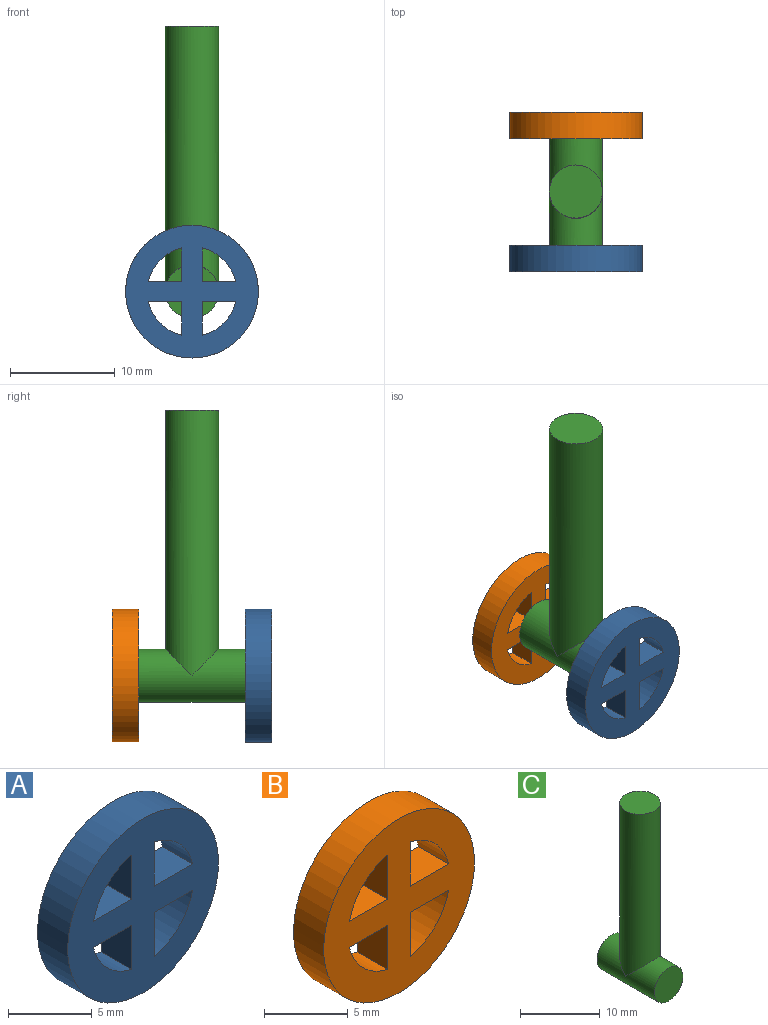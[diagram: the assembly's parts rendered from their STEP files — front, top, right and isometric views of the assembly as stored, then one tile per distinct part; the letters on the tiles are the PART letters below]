
ASSEMBLY  parts=3 mates=2
PART A: 15 faces, bbox 12.7x2.5x12.7 mm
  f0: cylinder r=4.28mm len=3.22mm, axis (0,1,0), area 12.2mm2, adj f1,f12,f13,f14
  f1: plane 3.22x2.54mm, normal (0,0,1), area 8.2mm2, adj f0,f12,f13,f14
  f2: cylinder r=4.28mm len=3.22mm, axis (0,1,0), area 12.2mm2, adj f3,f9,f13,f14
  f3: plane 3.22x2.54mm, normal (-1,0,0), area 8.2mm2, adj f2,f9,f13,f14
  f4: plane 3.22x2.54mm, normal (0,0,-1), area 8.2mm2, adj f5,f10,f13,f14
  f5: cylinder r=4.28mm len=3.22mm, axis (0,1,0), area 12.2mm2, adj f4,f10,f13,f14
  f6: cylinder r=4.28mm len=3.22mm, axis (0,1,0), area 12.2mm2, adj f7,f11,f13,f14
  f7: plane 3.22x2.54mm, normal (0,0,-1), area 8.2mm2, adj f6,f11,f13,f14
  f8: cylinder r=6.35mm len=12.7mm, axis (0,1,0), area 101.3mm2, adj f13,f14
  f9: plane 3.22x2.54mm, normal (0,0,1), area 8.2mm2, adj f2,f3,f13,f14
  f10: plane 3.22x2.54mm, normal (1,0,0), area 8.2mm2, adj f4,f5,f13,f14
  f11: plane 3.22x2.54mm, normal (-1,0,0), area 8.2mm2, adj f6,f7,f13,f14
  f12: plane 3.22x2.54mm, normal (1,0,0), area 8.2mm2, adj f0,f1,f13,f14
  f13: plane 12.7x12.7mm, normal (0,-1,0), area 97.9mm2, adj f0,f1,f2,f3,f4,f5,f6,f7
  f14: plane 12.7x12.7mm, normal (0,1,0), area 97.9mm2, adj f0,f1,f2,f3,f4,f5,f6,f7
PART B: 15 faces, bbox 12.7x2.5x12.7 mm
  f0: cylinder r=4.28mm len=3.22mm, axis (0,-1,0), area 12.2mm2, adj f1,f12,f13,f14
  f1: plane 3.22x2.54mm, normal (1,0,0), area 8.2mm2, adj f0,f12,f13,f14
  f2: cylinder r=4.28mm len=3.22mm, axis (0,-1,0), area 12.2mm2, adj f3,f9,f13,f14
  f3: plane 3.22x2.54mm, normal (0,0,1), area 8.2mm2, adj f2,f9,f13,f14
  f4: plane 3.22x2.54mm, normal (0,0,-1), area 8.2mm2, adj f5,f10,f13,f14
  f5: plane 3.22x2.54mm, normal (1,0,0), area 8.2mm2, adj f4,f10,f13,f14
  f6: cylinder r=4.28mm len=3.22mm, axis (0,-1,0), area 12.2mm2, adj f7,f11,f13,f14
  f7: plane 3.22x2.54mm, normal (-1,0,0), area 8.2mm2, adj f6,f11,f13,f14
  f8: cylinder r=6.35mm len=12.7mm, axis (0,-1,0), area 101.3mm2, adj f13,f14
  f9: plane 3.22x2.54mm, normal (-1,0,0), area 8.2mm2, adj f2,f3,f13,f14
  f10: cylinder r=4.28mm len=3.22mm, axis (0,-1,0), area 12.2mm2, adj f4,f5,f13,f14
  f11: plane 3.22x2.54mm, normal (0,0,-1), area 8.2mm2, adj f6,f7,f13,f14
  f12: plane 3.22x2.54mm, normal (0,0,1), area 8.2mm2, adj f0,f1,f13,f14
  f13: plane 12.7x12.7mm, normal (0,1,0), area 97.9mm2, adj f0,f1,f2,f3,f4,f5,f6,f7
  f14: plane 12.7x12.7mm, normal (0,-1,0), area 97.9mm2, adj f0,f1,f2,f3,f4,f5,f6,f7
PART C: 5 faces, bbox 5.1x10.2x27.9 mm
  f0: cylinder r=2.54mm len=25.4mm, axis (0,0,-1), area 379.6mm2, adj f1,f2
  f1: plane 5.08x5.08mm, normal (0,0,1), area 20.3mm2, adj f0
  f2: cylinder r=2.54mm len=10.16mm, axis (0,1,0), area 136.3mm2, adj f0,f3,f4
  f3: plane 5.08x5.08mm, normal (0,-1,0), area 20.3mm2, adj f2
  f4: plane 5.08x5.08mm, normal (0,1,0), area 20.3mm2, adj f2
PLACE A t=(-21.96,4.45,25.75)mm
PLACE B rot(axis=(1,0,0),180deg) t=(-21.96,17.15,25.75)mm
PLACE C t=(-21.96,4.45,25.75)mm
MATE revolute A.f2 <-> C.f2  axis (0,1,0) through (-21.96,-0.63,25.75)mm
MATE revolute B.f2 <-> C.f2  axis (0,-1,0) through (-21.96,9.53,25.75)mm
